FCSTD DOCUMENT  (FreeCAD 1.0R39319 (Git))
Label: sketch 1
License: All rights reserved
LicenseURL: https://en.wikipedia.org/wiki/All_rights_reserved
objects: Sketcher::SketchObject×1, PartDesign::Body×1
note: 3 computed .brp shape members not serialized (recipe doc carries the construction recipe); baked Part::Feature solids carry a one-line shape summary decoded from their .brp

FEATURE [Sketcher::SketchObject] Sketch
  ArcFitTolerance = 1e-06
  AttachmentSupport = -> [XY_Plane]
  FullyConstrained = true
  MakeInternals = false
  MapMode = 5
  sketch-geometry (20):
    g0: LineSegment StartX=-36 StartY=48 StartZ=0 EndX=-36 EndY=-48 EndZ=0
    g1: LineSegment StartX=-36 StartY=-48 StartZ=0 EndX=36 EndY=-48 EndZ=0
    g2: LineSegment StartX=36 StartY=-48 StartZ=0 EndX=36 EndY=48 EndZ=0
    g3: LineSegment StartX=36 StartY=48 StartZ=0 EndX=-36 EndY=48 EndZ=0
    g4: GeomPoint [constr] X=0 Y=0 Z=0
    g5: Circle CenterX=-26 CenterY=-18 CenterZ=0 NormalX=0 NormalY=0 NormalZ=1 AngleXU=0 Radius=3
    g6: Circle CenterX=0 CenterY=-18 CenterZ=0 NormalX=0 NormalY=0 NormalZ=1 AngleXU=0 Radius=14
    g7: Circle CenterX=26 CenterY=-18 CenterZ=0 NormalX=0 NormalY=0 NormalZ=1 AngleXU=0 Radius=3
    g8: Circle CenterX=-16 CenterY=-38 CenterZ=0 NormalX=0 NormalY=0 NormalZ=1 AngleXU=0 Radius=3
    g9: Circle CenterX=16 CenterY=-38 CenterZ=0 NormalX=0 NormalY=0 NormalZ=1 AngleXU=0 Radius=3
    g10: Circle CenterX=-16 CenterY=38 CenterZ=0 NormalX=0 NormalY=0 NormalZ=1 AngleXU=0 Radius=3
    g11: Circle CenterX=16 CenterY=38 CenterZ=0 NormalX=0 NormalY=0 NormalZ=1 AngleXU=0 Radius=3
    g12: ArcOfCircle CenterX=-16 CenterY=18 CenterZ=0 NormalX=0 NormalY=0 NormalZ=1 AngleXU=0 Radius=10 StartAngle=0.643501 EndAngle=2.49809
    g13: ArcOfCircle CenterX=16 CenterY=18 CenterZ=0 NormalX=0 NormalY=0 NormalZ=1 AngleXU=0 Radius=10 StartAngle=0.643501 EndAngle=2.49809
    g14: LineSegment StartX=-24 StartY=24 StartZ=0 EndX=-24 EndY=12 EndZ=0
    g15: LineSegment StartX=-8 StartY=24 StartZ=0 EndX=-8 EndY=12 EndZ=0
    g16: LineSegment StartX=8 StartY=24 StartZ=0 EndX=8 EndY=12 EndZ=0
    g17: LineSegment StartX=24 StartY=24 StartZ=0 EndX=24 EndY=12 EndZ=0
    g18: ArcOfCircle CenterX=-16 CenterY=18 CenterZ=0 NormalX=0 NormalY=0 NormalZ=1 AngleXU=0 Radius=10 StartAngle=3.78509 EndAngle=5.63968
    g19: ArcOfCircle CenterX=16 CenterY=18 CenterZ=0 NormalX=0 NormalY=0 NormalZ=1 AngleXU=0 Radius=10 StartAngle=3.78509 EndAngle=5.63968
  constraints (61):
    c: Coincident(g0,g1)
    c: Coincident(g1,g2)
    c: Coincident(g2,g3)
    c: Coincident(g3,g0)
    c: Vertical(g0)
    c: Vertical(g2)
    c: Horizontal(g1)
    c: Horizontal(g3)
    c: Symmetric(g2,g0,g4)
    c: Coincident(g4,g-1)
    c: DistanceX(g3,g3) = 72
    c: DistanceY(g2,g2) = 96
    c: PointOnObject(g6,g-2)
    c: Diameter(g6) = 28
    c: Distance(g6,g1) = 30
    c: Diameter(g5) = 6
    c: Distance(g5,g1) = 30
    c: Distance(g8,g1) = 10
    c: Distance(g7,g1) = 30
    c: Distance(g9,g1) = 10
    c: Distance(g5,g0) = 10
    c: Distance(g8,g0) = 20
    c: Distance(g7,g2) = 10
    c: Distance(g9,g2) = 20
    c: Diameter(g7) = 6
    c: Diameter(g8) = 6
    c: Diameter(g9) = 6
    c: Diameter(g10) = 6
    c: Equal(g10,g11)
    c: Horizontal(g10,g11)
    c: Distance(g11,g3) = 10
    c: Distance(g11,g2) = 20
    c: Distance(g10,g0) = 20
    c: Diameter(g12) = 20
    c: Equal(g12,g13)
    c: Horizontal(g12,g13)
    c: Vertical(g10,g12)
    c: Vertical(g11,g13)
    c: Distance(g12,g3) = 30
    c: Vertical(g14)
    c: Vertical(g15)
    c: PointOnObject(g14,g18)
    c: Distance(g15,g14) = 16
    c: Equal(g14,g15)
    c: Vertical(g16)
    c: Vertical(g17)
    c: PointOnObject(g16,g19)
    c: Distance(g17,g16) = 16
    c: Equal(g16,g17)
    c: Coincident(g18,g15)
    c: Coincident(g12,g15)
    c: Equal(g12,g18)
    c: Coincident(g12,g14)
    c: PointOnObject(g18,g14)
    c: Coincident(g12,g18)
    c: Coincident(g19,g17)
    c: Coincident(g13,g17)
    c: Equal(g13,g19)
    c: Coincident(g13,g16)
    c: PointOnObject(g19,g16)
    c: Coincident(g13,g19)
FEATURE [PartDesign::Body] Body
  AllowCompound = false
  Group = -> [Sketch]
  Origin = -> Origin
